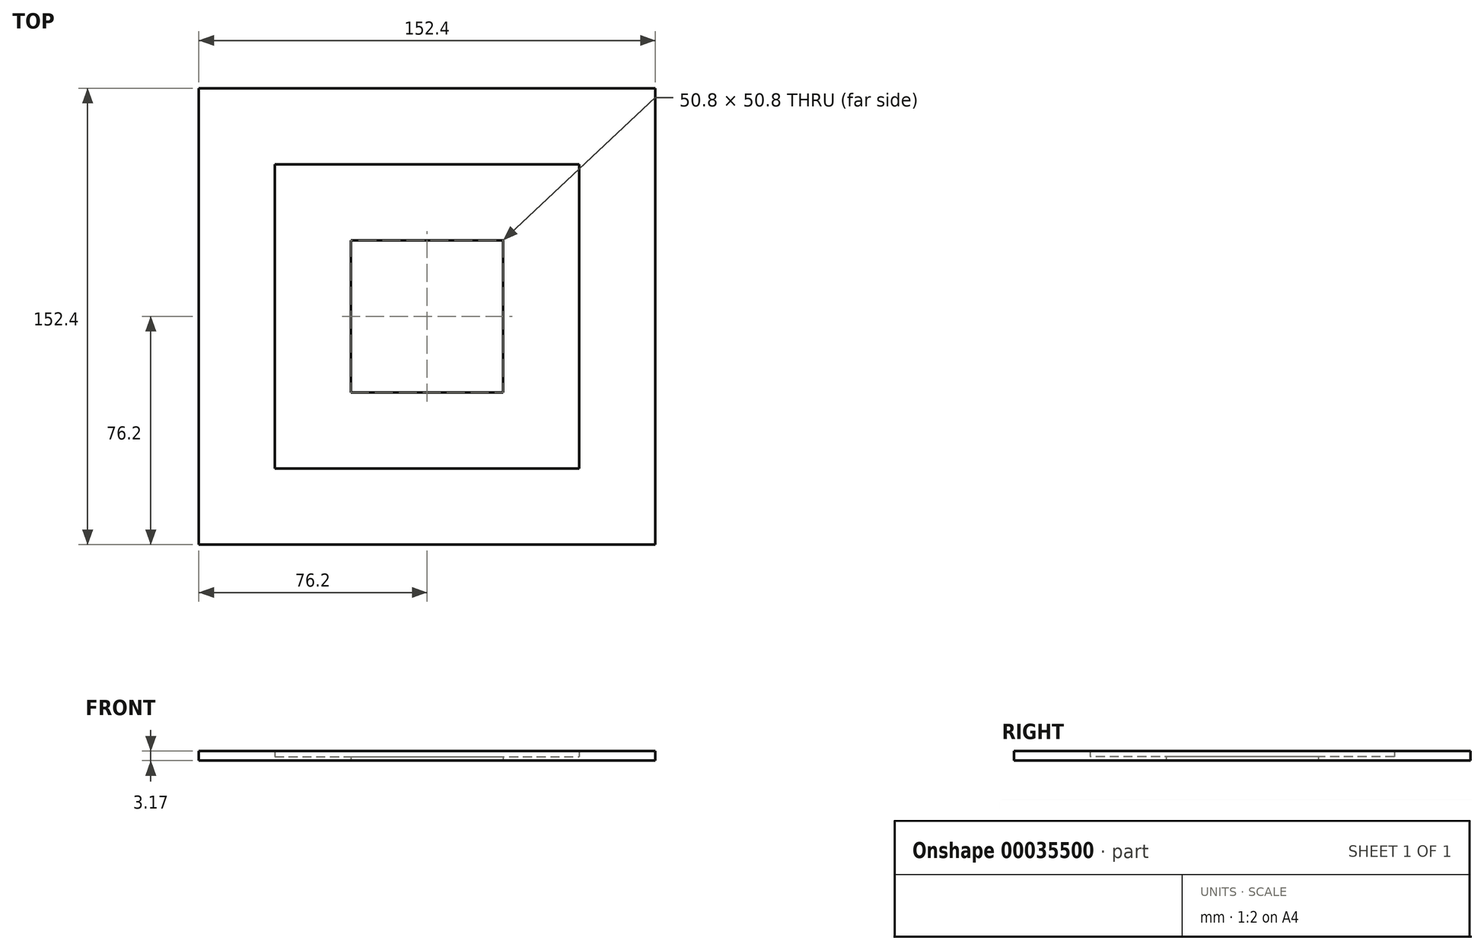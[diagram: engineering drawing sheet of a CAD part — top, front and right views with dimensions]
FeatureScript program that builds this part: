
annotation { "Feature Type Name" : "Feature", "Feature Type Description" : "" }
export const myFeature = defineFeature(function(context is Context, id is Id, definition is map)
    precondition{}
    {
        {
            var Q0;
            Q0=qCreatedBy(makeId("Top.planeOp"),FACE);
            var sketch = newSketch(context, id + "F0", { "sketchPlane" : qUnion([Q0])});
            skLineSegment(sketch, "E0.rect.bottom", {"start": v(76.2, 76.2) * mm, "end": v(-76.2, 76.2) * mm});
            skLineSegment(sketch, "E0.rect.top", {"start": v(76.2, -76.2) * mm, "end": v(-76.2, -76.2) * mm});
            skLineSegment(sketch, "E0.rect.left", {"start": v(76.2, 76.2) * mm, "end": v(76.2, -76.2) * mm});
            skLineSegment(sketch, "E0.rect.right", {"start": v(-76.2, 76.2) * mm, "end": v(-76.2, -76.2) * mm});
            skPoint(sketch, "E0.rect.middle", {"position": v(0, 0) * mm});
            skLineSegment(sketch, "E1.rect.bottom", {"start": v(-50.8, 50.8) * mm, "end": v(50.8, 50.8) * mm});
            skLineSegment(sketch, "E1.rect.top", {"start": v(-50.8, -50.8) * mm, "end": v(50.8, -50.8) * mm});
            skLineSegment(sketch, "E1.rect.left", {"start": v(-50.8, 50.8) * mm, "end": v(-50.8, -50.8) * mm});
            skLineSegment(sketch, "E1.rect.right", {"start": v(50.8, 50.8) * mm, "end": v(50.8, -50.8) * mm});
            skLineSegment(sketch, "E2.rect.bottom", {"start": v(-25.4, 25.4) * mm, "end": v(25.4, 25.4) * mm});
            skLineSegment(sketch, "E2.rect.top", {"start": v(-25.4, -25.4) * mm, "end": v(25.4, -25.4) * mm});
            skLineSegment(sketch, "E2.rect.left", {"start": v(-25.4, 25.4) * mm, "end": v(-25.4, -25.4) * mm});
            skLineSegment(sketch, "E2.rect.right", {"start": v(25.4, 25.4) * mm, "end": v(25.4, -25.4) * mm});
            skSolve(sketch);
        }
        {
            var Q0;
            Q0=makeQuery(id+"F0.imprint","IMPRINT",FACE,{"disambiguationData":[TD([[makeQuery(id+"F0.imprint","IMPRINT",EDGE,{"derivedFrom":sQuery(id+"F0.wireOp",EDGE,"E0.rect.bottom")}),1.0]])]});
            extrude(context, id + "F1", {"entities" : qUnion([Q0]), "depth" : 3.17 * mm});
        }
        {
            var Q0;
            Q0=makeQuery(id+"F0.imprint","IMPRINT",FACE,{"disambiguationData":[TD([[makeQuery(id+"F0.imprint","IMPRINT",EDGE,{"derivedFrom":sQuery(id+"F0.wireOp",EDGE,"E1.rect.bottom")}),-1.0]])]});
            extrude(context, id + "F2", {"entities" : qUnion([Q0]), "operationType" : NewBodyOperationType.ADD, "depth" : 1.27 * mm});
        }
    });
